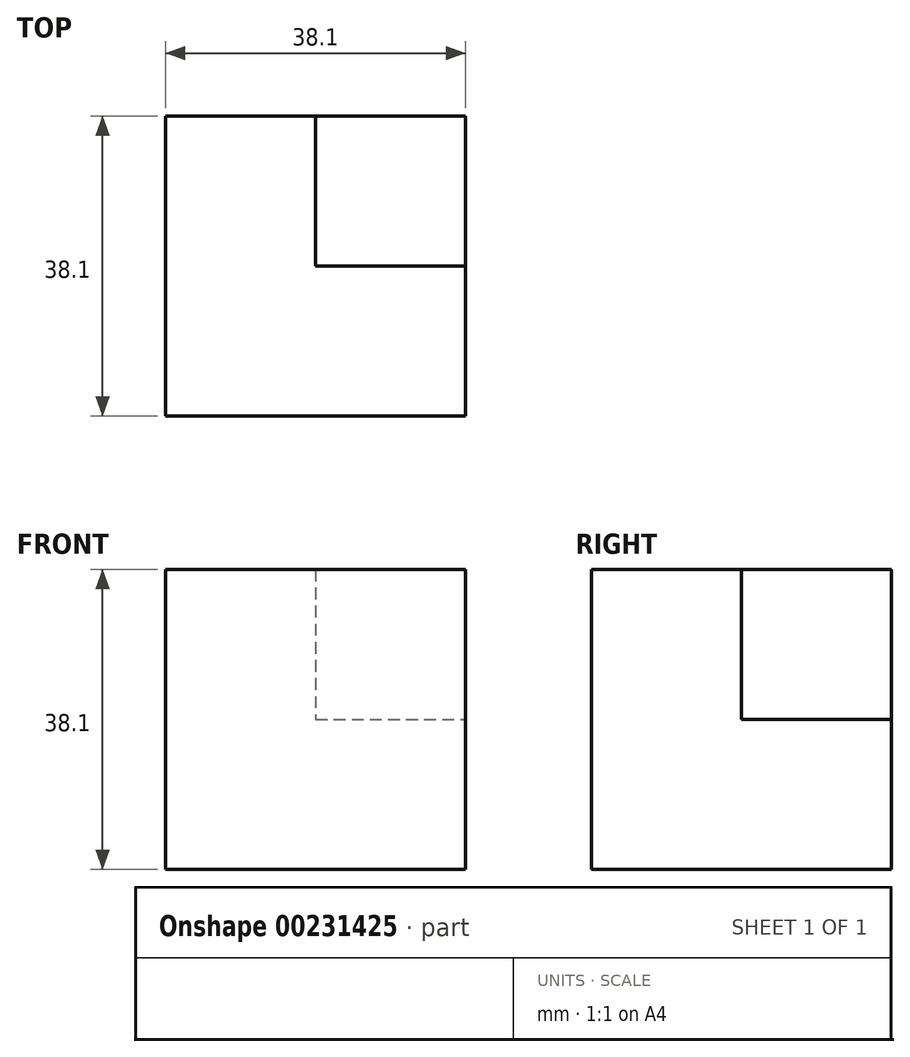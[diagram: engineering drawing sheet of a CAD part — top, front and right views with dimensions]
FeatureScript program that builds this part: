
annotation { "Feature Type Name" : "Feature", "Feature Type Description" : "" }
export const myFeature = defineFeature(function(context is Context, id is Id, definition is map)
    precondition{}
    {
        {
            var Q0;
            Q0=qCreatedBy(makeId("Front.planeOp"),FACE);
            var sketch = newSketch(context, id + "F0", { "sketchPlane" : qUnion([Q0])});
            skLineSegment(sketch, "E0.bottom", {"start": v(-16.54, 13.43) * mm, "end": v(2.51, 13.43) * mm});
            skLineSegment(sketch, "E0.top", {"start": v(-16.54, -24.67) * mm, "end": v(2.51, -24.67) * mm});
            skLineSegment(sketch, "E0.left", {"start": v(-16.54, 13.43) * mm, "end": v(-16.54, -24.67) * mm});
            skLineSegment(sketch, "E0.right", {"start": v(2.51, 13.43) * mm, "end": v(2.51, -24.67) * mm});
            skLineSegment(sketch, "E1.bottom", {"start": v(2.51, -24.67) * mm, "end": v(21.56, -24.67) * mm});
            skLineSegment(sketch, "E1.top", {"start": v(2.51, -5.62) * mm, "end": v(21.56, -5.62) * mm});
            skLineSegment(sketch, "E1.left", {"start": v(2.51, -24.67) * mm, "end": v(2.51, -5.62) * mm});
            skLineSegment(sketch, "E1.right", {"start": v(21.56, -24.67) * mm, "end": v(21.56, -5.62) * mm});
            skLineSegment(sketch, "E2.bottom", {"start": v(2.51, 13.43) * mm, "end": v(21.56, 13.43) * mm});
            skLineSegment(sketch, "E2.left", {"start": v(2.51, 13.43) * mm, "end": v(2.51, -5.62) * mm});
            skLineSegment(sketch, "E2.right", {"start": v(21.56, 13.43) * mm, "end": v(21.56, -5.62) * mm});
            skSolve(sketch);
        }
        {
            var Q0;
            Q0=makeQuery(id+"F0.imprint","IMPRINT",FACE,{"disambiguationData":[TD([[makeQuery(id+"F0.imprint","IMPRINT",EDGE,{"derivedFrom":sQuery(id+"F0.wireOp",EDGE,"E0.bottom")}),-1.0]])]});
            var Q1;
            Q1=makeQuery(id+"F0.imprint","IMPRINT",FACE,{"disambiguationData":[TD([[makeQuery(id+"F0.imprint","IMPRINT",EDGE,{"derivedFrom":sQuery(id+"F0.wireOp",EDGE,"E1.bottom")}),1.0]])]});
            var Q2;
            Q2=makeQuery(id+"F0.imprint","IMPRINT",FACE,{"disambiguationData":[TD([[makeQuery(id+"F0.imprint","IMPRINT",EDGE,{"derivedFrom":sQuery(id+"F0.wireOp",EDGE,"E2.bottom")}),-1.0]])]});
            extrude(context, id + "F1", {"entities" : qUnion([Q0, Q1, Q2]), "depth" : 19.05 * mm});
        }
        {
            var Q0;
            Q0=makeQuery(id+"F0.imprint","IMPRINT",FACE,{"disambiguationData":[TD([[makeQuery(id+"F0.imprint","IMPRINT",EDGE,{"derivedFrom":sQuery(id+"F0.wireOp",EDGE,"E0.bottom")}),-1.0]])]});
            var Q1;
            Q1=makeQuery(id+"F0.imprint","IMPRINT",FACE,{"disambiguationData":[TD([[makeQuery(id+"F0.imprint","IMPRINT",EDGE,{"derivedFrom":sQuery(id+"F0.wireOp",EDGE,"E1.bottom")}),1.0]])]});
            extrude(context, id + "F2", {"entities" : qUnion([Q0, Q1]), "operationType" : NewBodyOperationType.ADD, "oppositeDirection" : true, "depth" : 19.05 * mm});
        }
    });
